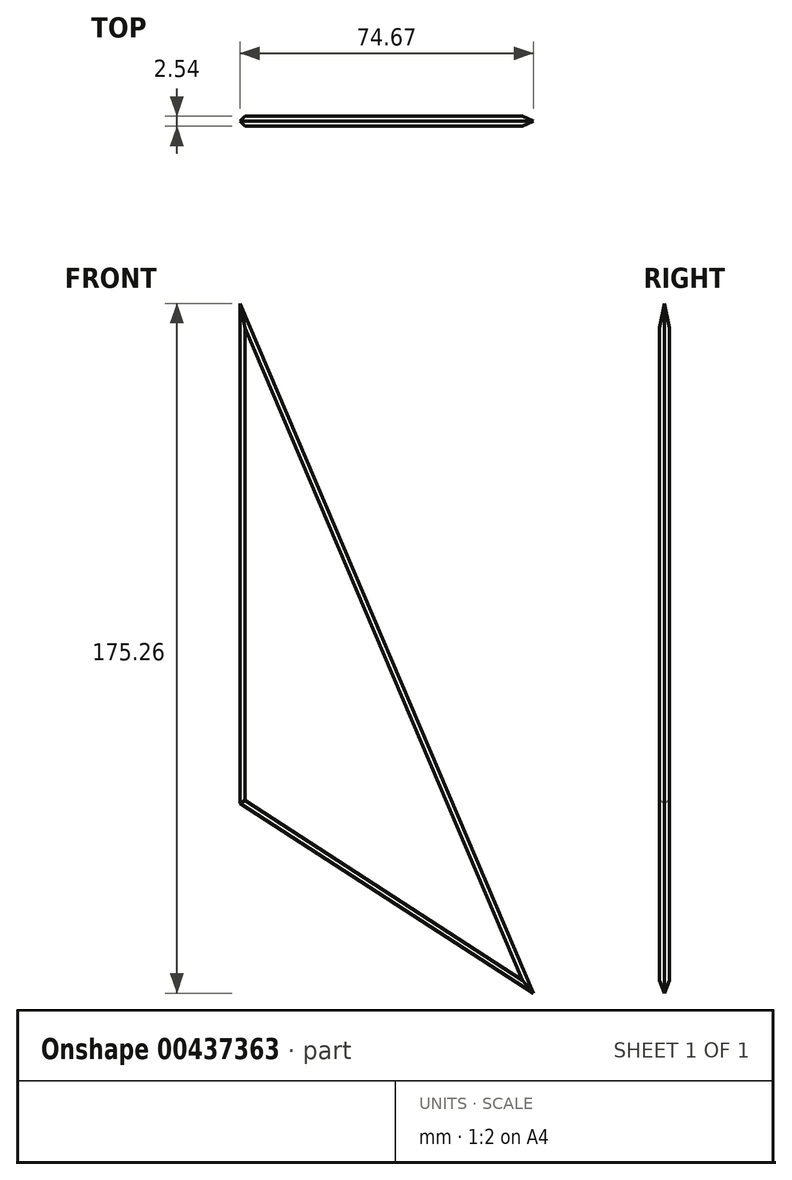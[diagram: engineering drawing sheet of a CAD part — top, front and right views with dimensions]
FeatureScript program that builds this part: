
annotation { "Feature Type Name" : "Feature", "Feature Type Description" : "" }
export const myFeature = defineFeature(function(context is Context, id is Id, definition is map)
    precondition{}
    {
        {
            var Q0;
            Q0=qCreatedBy(makeId("Front.planeOp"),FACE);
            var sketch = newSketch(context, id + "F0", { "sketchPlane" : qUnion([Q0])});
            skLineSegment(sketch, "E0", {"start": v(-54.16, 65.68) * mm, "end": v(-54.16, -61.32) * mm});
            skLineSegment(sketch, "E1", {"start": v(-54.16, 65.68) * mm, "end": v(20.5, -109.58) * mm});
            skLineSegment(sketch, "E2", {"start": v(20.5, -109.58) * mm, "end": v(-54.16, -61.32) * mm});
            skSolve(sketch);
        }
        {
            var Q0;
            Q0 = qSketchRegion(id + "F0", true);
            extrude(context, id + "F1", {"entities" : qUnion([Q0]), "depth" : 2.54 * mm});
        }
        {
            var Q0;
            Q0=makeQuery(id+"F1.opExtrude","CAP_FACE",FACE,{"disambiguationData":[OSD([sQuery(id+"F0.wireOp",EDGE,"E0"),sQuery(id+"F0.wireOp",EDGE,"E1"),sQuery(id+"F0.wireOp",EDGE,"E2")])],"isStart":false});
            var Q1;
            Q1=makeQuery(id+"F1.opExtrude","CAP_FACE",FACE,{"disambiguationData":[OSD([sQuery(id+"F0.wireOp",EDGE,"E0"),sQuery(id+"F0.wireOp",EDGE,"E1"),sQuery(id+"F0.wireOp",EDGE,"E2")])],"isStart":true});
            chamfer(context, id + "F2", {"entities" : qUnion([Q0, Q1]), "width" : 1.27 * mm, "tangentPropagation" : true});
        }
    });
